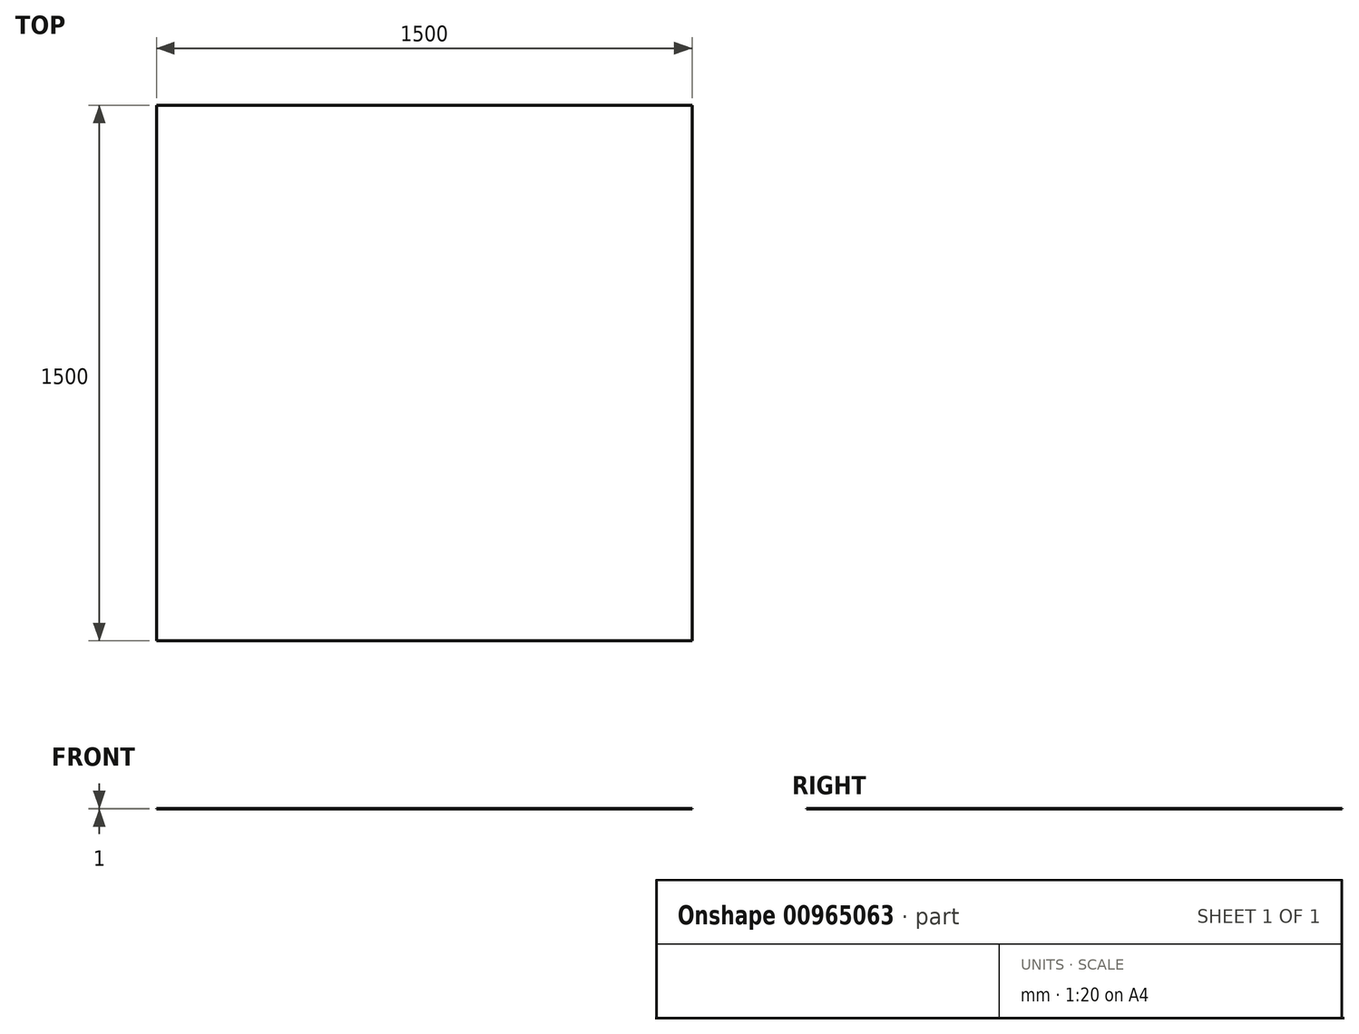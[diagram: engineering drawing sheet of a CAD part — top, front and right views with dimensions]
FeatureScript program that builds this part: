
annotation { "Feature Type Name" : "Feature", "Feature Type Description" : "" }
export const myFeature = defineFeature(function(context is Context, id is Id, definition is map)
    precondition{}
    {
        {
            var Q0;
            Q0=qCreatedBy(makeId("Top.planeOp"),FACE);
            var sketch = newSketch(context, id + "F0", { "sketchPlane" : qUnion([Q0])});
            skLineSegment(sketch, "E0.bottom", {"start": v(0, 0) * mm, "end": v(1500, 0) * mm});
            skLineSegment(sketch, "E0.top", {"start": v(0, 1500) * mm, "end": v(1500, 1500) * mm});
            skLineSegment(sketch, "E0.left", {"start": v(0, 0) * mm, "end": v(0, 1500) * mm});
            skLineSegment(sketch, "E0.right", {"start": v(1500, 0) * mm, "end": v(1500, 1500) * mm});
            skSolve(sketch);
        }
        {
            var Q0;
            Q0=makeQuery(id+"F0.imprint","IMPRINT",FACE,{"disambiguationData":[TD([[makeQuery(id+"F0.imprint","IMPRINT",EDGE,{"derivedFrom":sQuery(id+"F0.wireOp",EDGE,"E0.bottom")}),1.0]])]});
            extrude(context, id + "F1", {"entities" : qUnion([Q0]), "depth" : 1 * mm, "offsetDistance" : 25 * mm});
        }
    });
